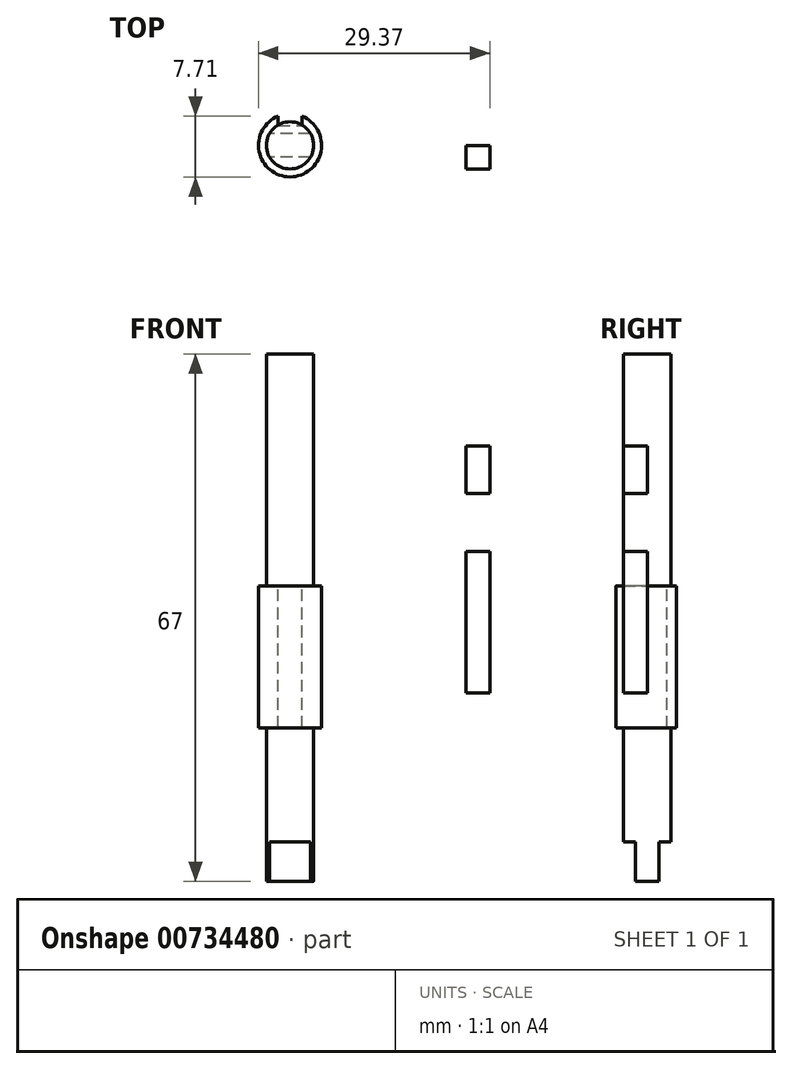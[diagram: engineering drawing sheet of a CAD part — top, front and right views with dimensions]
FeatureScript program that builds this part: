
annotation { "Feature Type Name" : "Feature", "Feature Type Description" : "" }
export const myFeature = defineFeature(function(context is Context, id is Id, definition is map)
    precondition{}
    {
        {
            var Q0;
            Q0=qCreatedBy(makeId("Front.planeOp"),FACE);
            var sketch = newSketch(context, id + "F0", { "sketchPlane" : qUnion([Q0])});
            skLineSegment(sketch, "E0", {"start": v(0, 55.8) * mm, "end": v(-3, 55.8) * mm});
            skLineSegment(sketch, "E1", {"start": v(-3, 55.8) * mm, "end": v(-3, 26.3) * mm});
            skLineSegment(sketch, "E2", {"start": v(-3, 26.3) * mm, "end": v(-4, 26.3) * mm});
            skLineSegment(sketch, "E3", {"start": v(-4, 26.3) * mm, "end": v(-4, 8.3) * mm});
            skLineSegment(sketch, "E4", {"start": v(-4, 8.3) * mm, "end": v(-3, 8.3) * mm});
            skLineSegment(sketch, "E5", {"start": v(-3, 8.3) * mm, "end": v(-3, -11.2) * mm});
            skLineSegment(sketch, "E6", {"start": v(-3, -11.2) * mm, "end": v(0, -11.2) * mm});
            skLineSegment(sketch, "E7", {"start": v(0, -11.2) * mm, "end": v(0, 55.8) * mm});
            skLineSegment(sketch, "E8", {"start": v(0, 44.92) * mm, "end": v(0, -14.5) * mm, "construction": true});
            skSolve(sketch);
        }
        {
            var Q0;
            Q0=makeQuery(id+"F0.imprint","IMPRINT",FACE,{"disambiguationData":[TD([[makeQuery(id+"F0.imprint","IMPRINT",EDGE,{"derivedFrom":sQuery(id+"F0.wireOp",EDGE,"E0")}),1.0]])]});
            var Q1;
            Q1=sQuery(id+"F0.wireOp",EDGE,"E8");
            revolve(context, id + "F1", {"surfaceOperationType" : NewSurfaceOperationType.NEW, "entities" : qUnion([Q0]), "axis" : qUnion([Q1]), "revolveType" : RevolveType.FULL});
        }
        {
            var Q0;
            Q0=makeQuery(id+"F1.opRevolve","SWEPT_FACE",FACE,{"disambiguationData":[OSD([sQuery(id+"F0.wireOp",EDGE,"E2")])]});
            var sketch = newSketch(context, id + "F2", { "sketchPlane" : qUnion([Q0])});
            skLineSegment(sketch, "E9.bottom", {"start": v(-1.5, 5.5) * mm, "end": v(1.5, 5.5) * mm});
            skLineSegment(sketch, "E9.top", {"start": v(-1.5, 2.5) * mm, "end": v(1.5, 2.5) * mm});
            skLineSegment(sketch, "E9.left", {"start": v(-1.5, 5.5) * mm, "end": v(-1.5, 2.5) * mm});
            skLineSegment(sketch, "E9.right", {"start": v(1.5, 5.5) * mm, "end": v(1.5, 2.5) * mm});
            skLineSegment(sketch, "E10", {"start": v(-2.32, 4) * mm, "end": v(2.46, 4) * mm, "construction": true});
            skSolve(sketch);
        }
        {
            var Q0;
            Q0 = qSketchRegion(id + "F2", true);
            extrude(context, id + "F3", {"entities" : qUnion([Q0]), "operationType" : NewBodyOperationType.REMOVE, "oppositeDirection" : true, "depth" : 18 * mm, "offsetDistance" : 25 * mm});
        }
        {
            var Q0;
            Q0=qCreatedBy(makeId("Front.planeOp"),FACE);
            var sketch = newSketch(context, id + "F4", { "sketchPlane" : qUnion([Q0])});
            skLineSegment(sketch, "E11.bottom", {"start": v(25.37, 44.09) * mm, "end": v(22.37, 44.09) * mm});
            skLineSegment(sketch, "E11.top", {"start": v(25.37, 38.09) * mm, "end": v(22.37, 38.09) * mm});
            skLineSegment(sketch, "E11.left", {"start": v(25.37, 44.09) * mm, "end": v(25.37, 38.09) * mm});
            skLineSegment(sketch, "E11.right", {"start": v(22.37, 44.09) * mm, "end": v(22.37, 38.09) * mm});
            skLineSegment(sketch, "E12.bottom", {"start": v(25.37, 30.71) * mm, "end": v(22.37, 30.71) * mm});
            skLineSegment(sketch, "E12.top", {"start": v(25.37, 12.71) * mm, "end": v(22.37, 12.71) * mm});
            skLineSegment(sketch, "E12.left", {"start": v(25.37, 30.71) * mm, "end": v(25.37, 12.71) * mm});
            skLineSegment(sketch, "E12.right", {"start": v(22.37, 30.71) * mm, "end": v(22.37, 12.71) * mm});
            skSolve(sketch);
        }
        {
            var Q0;
            Q0 = qSketchRegion(id + "F4", true);
            extrude(context, id + "F5", {"entities" : qUnion([Q0]), "depth" : 3 * mm, "offsetDistance" : 25 * mm});
        }
        {
            var Q0;
            Q0=makeQuery(id+"F1.opRevolve","SWEPT_FACE",FACE,{"disambiguationData":[OSD([sQuery(id+"F0.wireOp",EDGE,"E6")])]});
            var sketch = newSketch(context, id + "F6", { "sketchPlane" : qUnion([Q0])});
            skLineSegment(sketch, "E13", {"start": v(6.91, -3) * mm, "end": v(-8.02, -3) * mm, "construction": true});
            skLineSegment(sketch, "E14.bottom", {"start": v(5, -5.5) * mm, "end": v(-5, -5.5) * mm});
            skLineSegment(sketch, "E14.top", {"start": v(5, -1.5) * mm, "end": v(-5, -1.5) * mm});
            skLineSegment(sketch, "E14.left", {"start": v(5, -5.5) * mm, "end": v(5, -1.5) * mm});
            skLineSegment(sketch, "E14.right", {"start": v(-5, -5.5) * mm, "end": v(-5, -1.5) * mm});
            skLineSegment(sketch, "E15.MirrorCS", {"start": v(5, 5.5) * mm, "end": v(5, 1.5) * mm});
            skLineSegment(sketch, "E16.MirrorCS", {"start": v(-5, 5.5) * mm, "end": v(-5, 1.5) * mm});
            skLineSegment(sketch, "E17.MirrorCS", {"start": v(5, 5.5) * mm, "end": v(-5, 5.5) * mm});
            skLineSegment(sketch, "E18.MirrorCS", {"start": v(5, 1.5) * mm, "end": v(-5, 1.5) * mm});
            skSolve(sketch);
        }
        {
            var Q0;
            Q0 = qSketchRegion(id + "F6", true);
            extrude(context, id + "F7", {"entities" : qUnion([Q0]), "operationType" : NewBodyOperationType.REMOVE, "oppositeDirection" : true, "depth" : 5 * mm, "offsetDistance" : 25 * mm});
        }
    });
